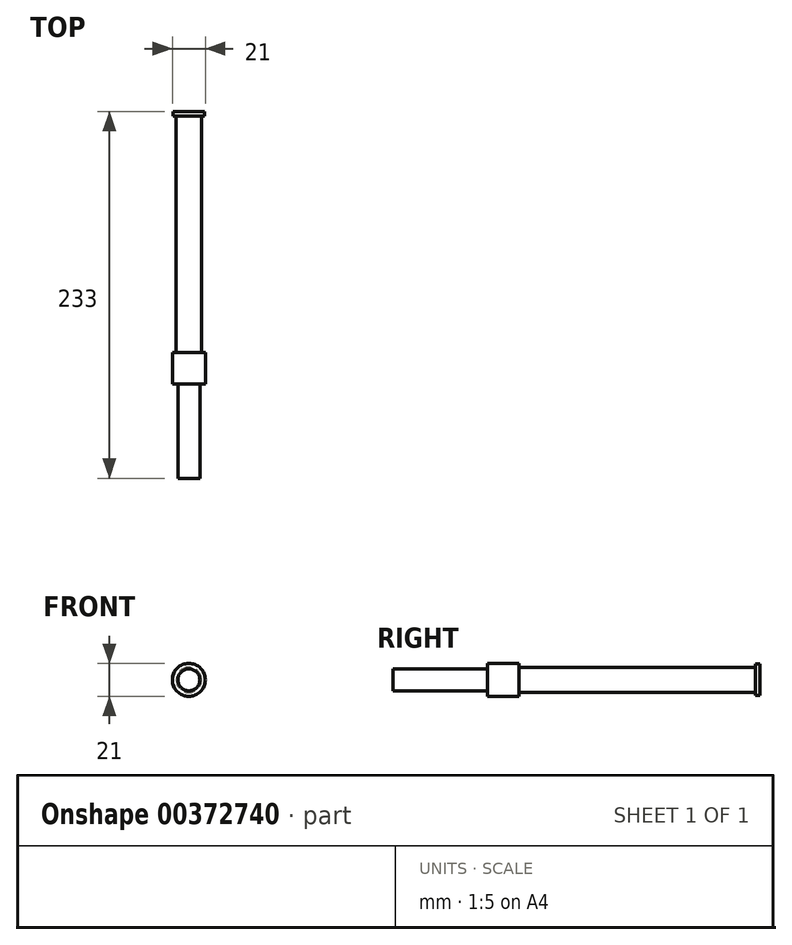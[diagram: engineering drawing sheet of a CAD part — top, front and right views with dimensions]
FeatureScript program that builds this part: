
annotation { "Feature Type Name" : "Feature", "Feature Type Description" : "" }
export const myFeature = defineFeature(function(context is Context, id is Id, definition is map)
    precondition{}
    {
        {
            var Q0;
            Q0=qCreatedBy(makeId("Front.planeOp"),FACE);
            var sketch = newSketch(context, id + "F0", { "sketchPlane" : qUnion([Q0])});
            skCircle(sketch, "E0", {"center": v(0, 0) * mm, "radius": 10.5 * mm});
            skSolve(sketch);
        }
        {
            var Q0;
            Q0 = qSketchRegion(id + "F0", true);
            extrude(context, id + "F1", {"entities" : qUnion([Q0]), "depth" : 20 * mm});
        }
        {
            var Q0;
            Q0=makeQuery(id+"F1.opExtrude","CAP_FACE",FACE,{"disambiguationData":[OSD([sQuery(id+"F0.wireOp",EDGE,"E0")])],"isStart":false});
            var sketch = newSketch(context, id + "F2", { "sketchPlane" : qUnion([Q0])});
            skCircle(sketch, "E1", {"center": v(0, 0) * mm, "radius": 7 * mm});
            skSolve(sketch);
        }
        {
            var Q0;
            Q0 = qSketchRegion(id + "F2", true);
            extrude(context, id + "F3", {"entities" : qUnion([Q0]), "operationType" : NewBodyOperationType.ADD, "depth" : 60 * mm});
        }
        {
            var Q0;
            Q0=makeQuery(id+"F1.opExtrude","CAP_FACE",FACE,{"disambiguationData":[OSD([sQuery(id+"F0.wireOp",EDGE,"E0")])],"isStart":true});
            var sketch = newSketch(context, id + "F4", { "sketchPlane" : qUnion([Q0])});
            skCircle(sketch, "E2", {"center": v(0, 0) * mm, "radius": 8 * mm});
            skSolve(sketch);
        }
        {
            var Q0;
            Q0 = qSketchRegion(id + "F4", true);
            var sketch = newSketch(context, id + "F5", { "sketchPlane" : qUnion([Q0])});
            skSolve(sketch);
        }
        {
            var Q0;
            Q0 = qSketchRegion(id + "F4", true);
            var Q1;
            Q1=makeQuery(id+"F5.imprint","IMPRINT",FACE,{"disambiguationData":[TD([[makeQuery(id+"F5.imprint","IMPRINT",EDGE,{"derivedFrom":makeQuery(id+"F4.imprint","IMPRINT",EDGE,{"derivedFrom":sQuery(id+"F4.wireOp",EDGE,"E2")})}),1.0]])]});
            extrude(context, id + "F6", {"entities" : qUnion([Q0, Q1]), "operationType" : NewBodyOperationType.ADD, "depth" : 150 * mm});
        }
        {
            var Q0;
            {var subQ0=sQuery(id+"F4.wireOp",EDGE,"E2");Q0=makeQuery(id+"F6.opExtrude","CAP_FACE",FACE,{"disambiguationData":[OSD([subQ0]),TDD([makeQuery(id+"F4.imprint","IMPRINT",EDGE,{"derivedFrom":subQ0})])],"isStart":false});}
            var sketch = newSketch(context, id + "F7", { "sketchPlane" : qUnion([Q0])});
            skCircle(sketch, "E3", {"center": v(0, 0) * mm, "radius": 10 * mm});
            skSolve(sketch);
        }
        {
            var Q0;
            Q0 = qSketchRegion(id + "F7", true);
            extrude(context, id + "F8", {"entities" : qUnion([Q0]), "operationType" : NewBodyOperationType.ADD, "depth" : 3 * mm});
        }
    });
